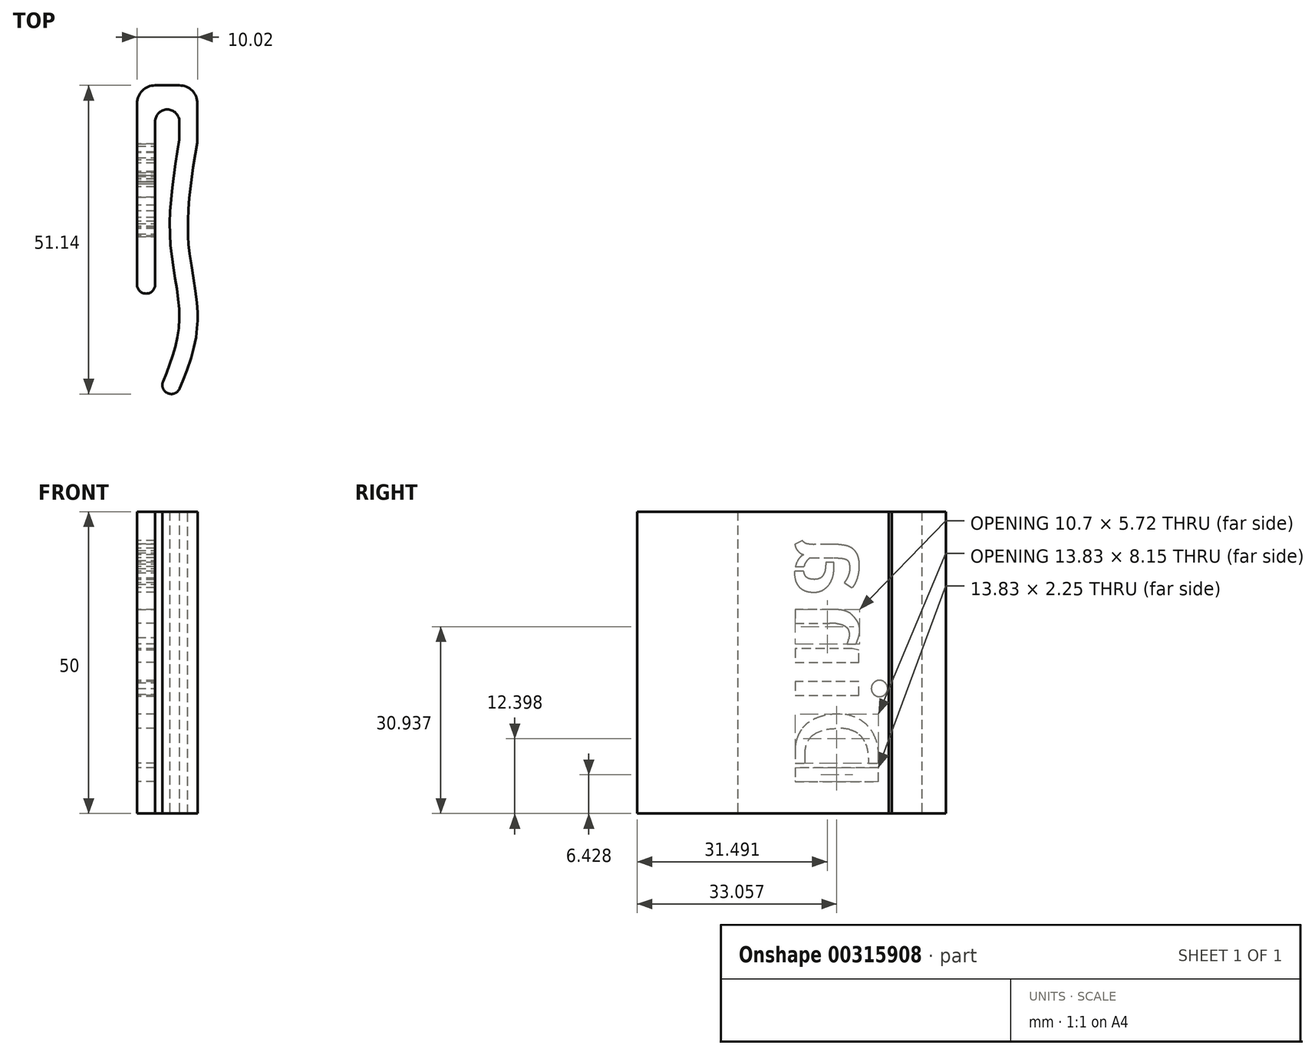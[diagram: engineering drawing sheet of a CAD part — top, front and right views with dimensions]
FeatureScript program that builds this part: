
annotation { "Feature Type Name" : "Feature", "Feature Type Description" : "" }
export const myFeature = defineFeature(function(context is Context, id is Id, definition is map)
    precondition{}
    {
        {
            var Q0;
            Q0=qCreatedBy(makeId("Top.planeOp"),FACE);
            var sketch = newSketch(context, id + "F0", { "sketchPlane" : qUnion([Q0])});
            skLineSegment(sketch, "E0.left", {"start": v(-12, 17.66) * mm, "end": v(-12, -12.34) * mm});
            skLineSegment(sketch, "E0.right", {"start": v(-9, 14.66) * mm, "end": v(-9, -12.34) * mm});
            skLineSegment(sketch, "E1.right", {"start": v(-2, 17.66) * mm, "end": v(-2, 14.66) * mm});
            skLineSegment(sketch, "E2.left", {"start": v(-2, 14.66) * mm, "end": v(-2, 11.66) * mm});
            skLineSegment(sketch, "E2.right", {"start": v(-5, 14.66) * mm, "end": v(-5, 11.66) * mm});
            skFitSpline(sketch, "E3", {"points": [v(-5, 11.66) * mm, v(-6.5, -5.15) * mm, v(-5, -18.43) * mm, v(-7.7, -28.42) * mm], "startDerivative": vector(-7.44, -45.92) * mm, "endDerivative": vector(-13.16, -32.95) * mm});
            skFitSpline(sketch, "E4.0", {"points": [v(-2.04, 11.18) * mm, v(-2.35, 9.27) * mm, v(-2.81, 6.43) * mm, v(-3.27, 2.76) * mm, v(-3.47, 0.53) * mm, v(-3.56, -1.21) * mm, v(-3.59, -2.5) * mm, v(-3.57, -3.54) * mm, v(-3.54, -4.37) * mm, v(-3.5, -5.19) * mm, v(-3.4, -6.2) * mm, v(-3.2, -7.86) * mm, v(-2.88, -9.94) * mm, v(-2.46, -12.48) * mm, v(-2.17, -14.63) * mm, v(-2.02, -16.37) * mm, v(-1.99, -17.48) * mm, v(-2, -18.37) * mm, v(-2.04, -19.27) * mm, v(-2.15, -20.36) * mm, v(-2.35, -21.64) * mm, v(-2.7, -23.28) * mm, v(-3.28, -25.23) * mm, v(-4.09, -27.44) * mm, v(-4.65, -28.85) * mm, v(-4.92, -29.53) * mm]});
            skArc(sketch, "E5", {"start": v(-7.7, -28.42) * mm, "mid": v(-6.87, -30.37) * mm, "end": v(-4.92, -29.53) * mm});
            skArc(sketch, "E6", {"start": v(-12, -12.34) * mm, "mid": v(-10.5, -13.84) * mm, "end": v(-9, -12.34) * mm});
            skLineSegment(sketch, "E7", {"start": v(-2.04, 11.18) * mm, "end": v(-2, 11.66) * mm});
            skArc(sketch, "E8", {"start": v(-9, 14.66) * mm, "mid": v(-7, 16.66) * mm, "end": v(-5, 14.66) * mm});
            skLineSegment(sketch, "E9", {"start": v(-9, 20.66) * mm, "end": v(-5, 20.66) * mm});
            skArc(sketch, "E10", {"start": v(-12, 17.66) * mm, "mid": v(-11.12, 19.78) * mm, "end": v(-9, 20.66) * mm});
            skArc(sketch, "E11", {"start": v(-5, 20.66) * mm, "mid": v(-2.88, 19.78) * mm, "end": v(-2, 17.66) * mm});
            skSolve(sketch);
        }
        {
            var Q0;
            Q0 = qSketchRegion(id + "F0", true);
            extrude(context, id + "F1", {"entities" : qUnion([Q0]), "endBound" : BoundingType.SYMMETRIC, "depth" : 50 * mm});
        }
        {
            var Q0;
            Q0=makeQuery(id+"F1.opExtrude","SWEPT_FACE",FACE,{"disambiguationData":[OSD([sQuery(id+"F0.wireOp",EDGE,"E0.left")])]});
            var sketch = newSketch(context, id + "F2", { "sketchPlane" : qUnion([Q0])});
            skText(sketch, "E12", { "text": "Dina", "fontName": "AllertaStencil-Regular.ttf"});
            const initialGuessF2  = {"E12": [0.00434, -0.0215, 0, 1, 0.01384]};
            skSetInitialGuess(sketch, initialGuessF2);
            skSolve(sketch);
        }
        {
            var Q0;
            Q0 = qSketchRegion(id + "F2", true);
            extrude(context, id + "F3", {"entities" : qUnion([Q0]), "operationType" : NewBodyOperationType.REMOVE, "endBound" : BoundingType.UP_TO_NEXT, "oppositeDirection" : true, "depth" : 25 * mm});
        }
    });
